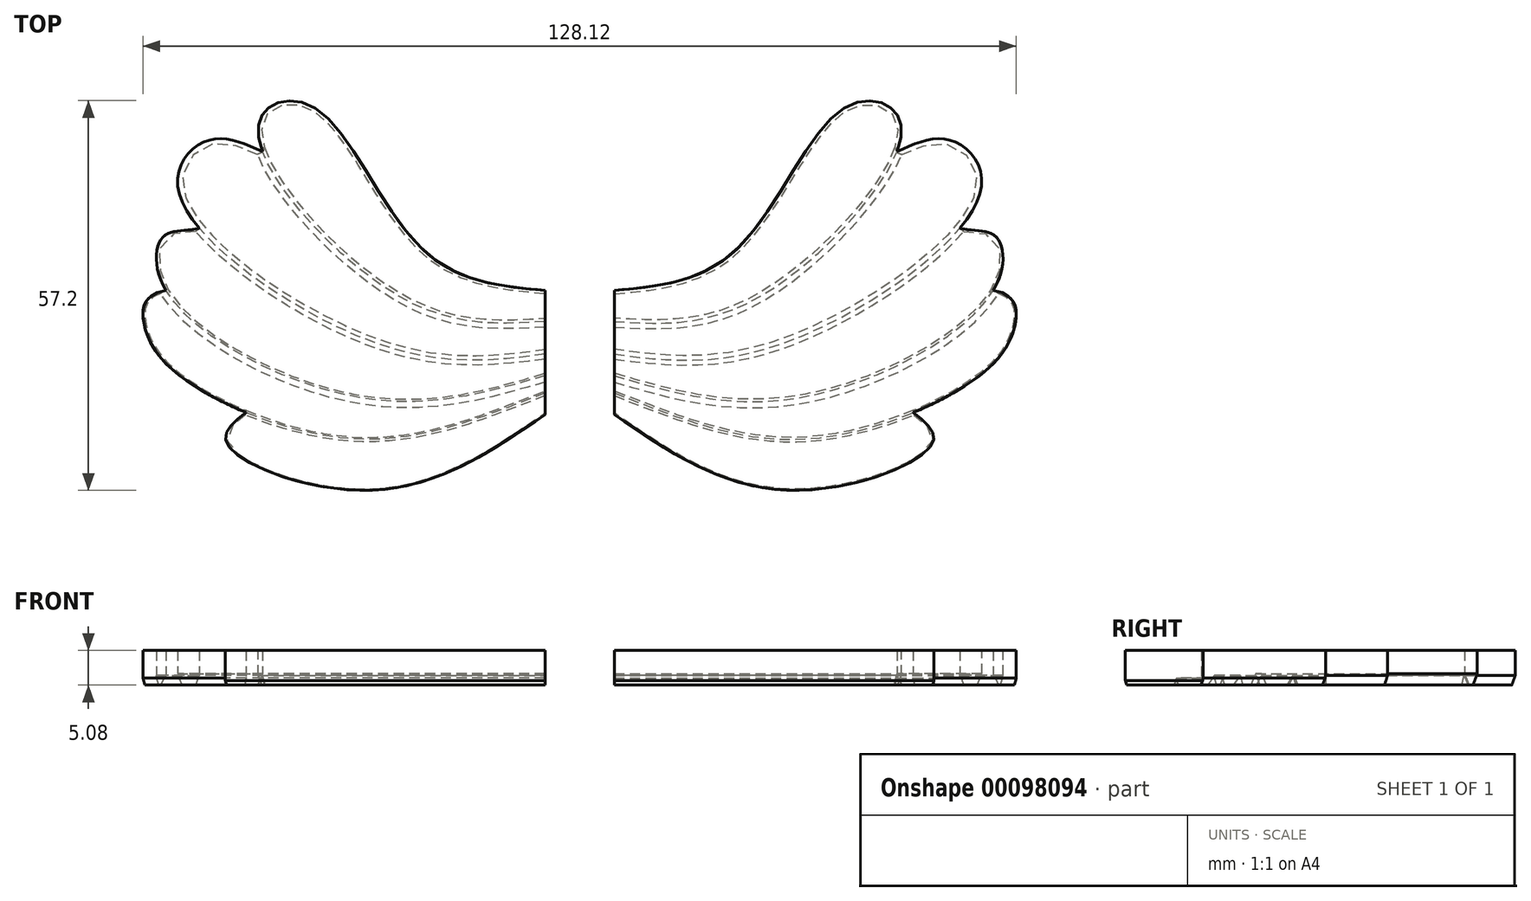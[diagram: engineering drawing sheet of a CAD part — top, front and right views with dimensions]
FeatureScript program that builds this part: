
annotation { "Feature Type Name" : "Feature", "Feature Type Description" : "" }
export const myFeature = defineFeature(function(context is Context, id is Id, definition is map)
    precondition{}
    {
        {
            var Q0;
            Q0=qCreatedBy(makeId("Top.planeOp"),FACE);
            var sketch = newSketch(context, id + "F0", { "sketchPlane" : qUnion([Q0])});
            skFitSpline(sketch, "E0", {"points": [v(0, 19.27) * mm, v(17.8, 25.14) * mm, v(33.22, 45.7) * mm, v(40.56, 46.06) * mm, v(41.47, 39.64) * mm, v(20, 17.61) * mm, v(0, 14.68) * mm], "startDerivative": vector(108.48, 9.49) * mm, "endDerivative": vector(-105.45, 6.4) * mm});
            skFitSpline(sketch, "E1", {"points": [v(41.47, 39.64) * mm, v(49.36, 41.29) * mm, v(53.77, 33.95) * mm, v(24.4, 11.38) * mm, v(0, 9.9) * mm], "startDerivative": vector(47.31, 21.5) * mm, "endDerivative": vector(-74.54, 9.85) * mm});
            skFitSpline(sketch, "E2", {"points": [v(50.7, 28.38) * mm, v(55.76, 27.32) * mm, v(55.6, 19.27) * mm, v(26.98, 3.48) * mm, v(0, 6.75) * mm], "startDerivative": vector(36.9, -10.53) * mm, "endDerivative": vector(-75.88, 22.36) * mm});
            skFitSpline(sketch, "E3", {"points": [v(55.6, 19.27) * mm, v(58.72, 13.94) * mm, v(53.4, 6.6) * mm, v(27.7, -2.57) * mm, v(0, 4.18) * mm], "startDerivative": vector(70.64, -12.37) * mm, "endDerivative": vector(-81.2, 31.3) * mm});
            skFitSpline(sketch, "E4", {"points": [v(43.84, 1.33) * mm, v(46.8, -2.94) * mm, v(26.24, -10.1) * mm, v(0, 1.04) * mm], "startDerivative": vector(28.2, -22.02) * mm, "endDerivative": vector(-55.4, 38.1) * mm});
            skLineSegment(sketch, "E5", {"start": v(0, 19.27) * mm, "end": v(0, 1.04) * mm});
            skSolve(sketch);
        }
        {
            var Q0;
            {var subQ0=sQuery(id+"F0.wireOp",EDGE,"E5");var subQ1=sQuery(id+"F0.wireOp",EDGE,"E0");var subQ2=makeQuery(id+"F0.imprint","INTERSECT",VERTEX,{"disambiguationData":[OD(0.0)],"derivedFrom":[subQ1,subQ0]});Q0=makeQuery(id+"F0.imprint","IMPRINT",FACE,{"disambiguationData":[TD([[makeQuery(id+"F0.imprint","IMPRINT",EDGE,{"disambiguationData":[TD([[subQ2,-1.0]])],"derivedFrom":subQ1}),-1.0]])]});}
            var Q1;
            {var subQ0=sQuery(id+"F0.wireOp",EDGE,"E5");var subQ1=sQuery(id+"F0.wireOp",EDGE,"E0");var subQ2=makeQuery(id+"F0.imprint","INTERSECT",VERTEX,{"disambiguationData":[OD(1.0)],"derivedFrom":[subQ1,subQ0]});Q1=makeQuery(id+"F0.imprint","IMPRINT",FACE,{"disambiguationData":[TD([[makeQuery(id+"F0.imprint","IMPRINT",EDGE,{"disambiguationData":[TD([[subQ2,1.0]])],"derivedFrom":subQ1}),1.0]])]});}
            var Q2;
            {var subQ0=sQuery(id+"F0.wireOp",EDGE,"E5");var subQ1=sQuery(id+"F0.wireOp",EDGE,"E1");var subQ2=makeQuery(id+"F0.imprint","INTERSECT",VERTEX,{"derivedFrom":[subQ1,subQ0]});Q2=makeQuery(id+"F0.imprint","IMPRINT",FACE,{"disambiguationData":[TD([[makeQuery(id+"F0.imprint","IMPRINT",EDGE,{"disambiguationData":[TD([[subQ2,1.0]])],"derivedFrom":subQ1}),1.0]])]});}
            var Q3;
            {var subQ0=sQuery(id+"F0.wireOp",EDGE,"E5");var subQ1=sQuery(id+"F0.wireOp",EDGE,"E2");var subQ2=makeQuery(id+"F0.imprint","INTERSECT",VERTEX,{"derivedFrom":[subQ1,subQ0]});Q3=makeQuery(id+"F0.imprint","IMPRINT",FACE,{"disambiguationData":[TD([[makeQuery(id+"F0.imprint","IMPRINT",EDGE,{"disambiguationData":[TD([[subQ2,1.0]])],"derivedFrom":subQ1}),1.0]])]});}
            var Q4;
            {var subQ3=sQuery(id+"F0.wireOp",EDGE,"E4");Q4=makeQuery(id+"F0.imprint","IMPRINT",FACE,{"disambiguationData":[TD([[makeQuery(id+"F0.imprint","IMPRINT",EDGE,{"derivedFrom":subQ3}),-1.0]])]});}
            extrude(context, id + "F1", {"entities" : qUnion([Q0, Q1, Q2, Q3, Q4]), "depth" : 5.08 * mm});
        }
        {
            var Q0;
            Q0=qCreatedBy(makeId("Right.planeOp"),FACE);
            var sketch = newSketch(context, id + "F2", { "sketchPlane" : qUnion([Q0])});
            skLineSegment(sketch, "E6", {"start": v(15.28, -0.28) * mm, "end": v(13.71, -0.28) * mm});
            skLineSegment(sketch, "E7", {"start": v(13.71, -0.28) * mm, "end": v(14.68, 1.45) * mm});
            skLineSegment(sketch, "E8", {"start": v(14.68, 1.45) * mm, "end": v(15.28, -0.28) * mm});
            skLineSegment(sketch, "E9", {"start": v(10.7, -0.27) * mm, "end": v(9.07, -0.27) * mm});
            skLineSegment(sketch, "E10", {"start": v(9.07, -0.27) * mm, "end": v(9.9, 1.64) * mm});
            skLineSegment(sketch, "E11", {"start": v(9.9, 1.64) * mm, "end": v(10.7, -0.27) * mm});
            skLineSegment(sketch, "E12", {"start": v(5.66, -0.2) * mm, "end": v(6.75, 1.43) * mm});
            skLineSegment(sketch, "E13", {"start": v(6.75, 1.43) * mm, "end": v(7.14, -0.2) * mm});
            skLineSegment(sketch, "E14", {"start": v(7.14, -0.2) * mm, "end": v(5.66, -0.2) * mm});
            skLineSegment(sketch, "E15", {"start": v(4.58, -0.33) * mm, "end": v(4.18, 1.05) * mm});
            skLineSegment(sketch, "E16", {"start": v(4.18, 1.05) * mm, "end": v(3.67, -0.33) * mm});
            skLineSegment(sketch, "E17", {"start": v(3.67, -0.33) * mm, "end": v(4.58, -0.33) * mm});
            skLineSegment(sketch, "E18", {"start": v(0.52, -0.3) * mm, "end": v(1.37, -0.3) * mm});
            skLineSegment(sketch, "E19", {"start": v(1.37, -0.3) * mm, "end": v(1.04, 0.64) * mm});
            skLineSegment(sketch, "E20", {"start": v(1.04, 0.64) * mm, "end": v(0.52, -0.3) * mm});
            skSolve(sketch);
        }
        {
            var Q0;
            Q0=makeQuery(id+"F2.imprint","IMPRINT",FACE,{"disambiguationData":[TD([[makeQuery(id+"F2.imprint","IMPRINT",EDGE,{"derivedFrom":sQuery(id+"F2.wireOp",EDGE,"E6")}),-1.0]])]});
            var Q1;
            Q1=sQuery(id+"F0.wireOp",EDGE,"E0");
            sweep(context, id + "F3", {"operationType" : NewBodyOperationType.REMOVE, "profiles" : qUnion([Q0]), "path" : qUnion([Q1])});
        }
        {
            var Q0;
            Q0=makeQuery(id+"F2.imprint","IMPRINT",FACE,{"disambiguationData":[TD([[makeQuery(id+"F2.imprint","IMPRINT",EDGE,{"derivedFrom":sQuery(id+"F2.wireOp",EDGE,"E9")}),-1.0]])]});
            var Q1;
            Q1=sQuery(id+"F0.wireOp",EDGE,"E1");
            sweep(context, id + "F4", {"operationType" : NewBodyOperationType.REMOVE, "profiles" : qUnion([Q0]), "path" : qUnion([Q1])});
        }
        {
            var Q0;
            Q0=makeQuery(id+"F2.imprint","IMPRINT",FACE,{"disambiguationData":[TD([[makeQuery(id+"F2.imprint","IMPRINT",EDGE,{"derivedFrom":sQuery(id+"F2.wireOp",EDGE,"E12")}),-1.0]])]});
            var Q1;
            Q1=sQuery(id+"F0.wireOp",EDGE,"E2");
            sweep(context, id + "F5", {"operationType" : NewBodyOperationType.REMOVE, "profiles" : qUnion([Q0]), "path" : qUnion([Q1])});
        }
        {
            var Q0;
            Q0=makeQuery(id+"F2.imprint","IMPRINT",FACE,{"disambiguationData":[TD([[makeQuery(id+"F2.imprint","IMPRINT",EDGE,{"derivedFrom":sQuery(id+"F2.wireOp",EDGE,"E15")}),1.0]])]});
            var Q1;
            Q1=sQuery(id+"F0.wireOp",EDGE,"E3");
            sweep(context, id + "F6", {"operationType" : NewBodyOperationType.REMOVE, "profiles" : qUnion([Q0]), "path" : qUnion([Q1])});
        }
        {
            var Q0;
            Q0=makeQuery(id+"F2.imprint","IMPRINT",FACE,{"disambiguationData":[TD([[makeQuery(id+"F2.imprint","IMPRINT",EDGE,{"derivedFrom":sQuery(id+"F2.wireOp",EDGE,"E18")}),1.0]])]});
            var Q1;
            Q1=sQuery(id+"F0.wireOp",EDGE,"E4");
            sweep(context, id + "F7", {"operationType" : NewBodyOperationType.REMOVE, "profiles" : qUnion([Q0]), "path" : qUnion([Q1])});
        }
        {
            var Q0;
            Q0=makeQuery(id+"F1.opExtrude","SWEPT_BODY",BODY,{"disambiguationData":[OSD([sQuery(id+"F0.wireOp",EDGE,"E0"),sQuery(id+"F0.wireOp",EDGE,"E1"),sQuery(id+"F0.wireOp",EDGE,"E2"),sQuery(id+"F0.wireOp",EDGE,"E3"),sQuery(id+"F0.wireOp",EDGE,"E4"),sQuery(id+"F0.wireOp",EDGE,"E5")])]});
            var Q1;
            Q1=qCreatedBy(makeId("Right.planeOp"),FACE);
            transform(context, id + "F8", {"entities" : qUnion([Q0]), "transformType" : TransformType.TRANSLATION_DISTANCE, "transformDirection" : qUnion([Q1]), "distance" : 5.08 * mm, "makeCopy" : false});
        }
        {
            var Q0;
            Q0=makeQuery(id+"F1.opExtrude","SWEPT_BODY",BODY,{"disambiguationData":[OSD([sQuery(id+"F0.wireOp",EDGE,"E0"),sQuery(id+"F0.wireOp",EDGE,"E1"),sQuery(id+"F0.wireOp",EDGE,"E2"),sQuery(id+"F0.wireOp",EDGE,"E3"),sQuery(id+"F0.wireOp",EDGE,"E4"),sQuery(id+"F0.wireOp",EDGE,"E5")])]});
            var Q1;
            Q1=qCreatedBy(makeId("Right.planeOp"),FACE);
            mirror(context, id + "F9", {"operationType" : NewBodyOperationType.ADD, "entities" : qUnion([Q0]), "mirrorPlane" : qUnion([Q1])});
        }
    });
